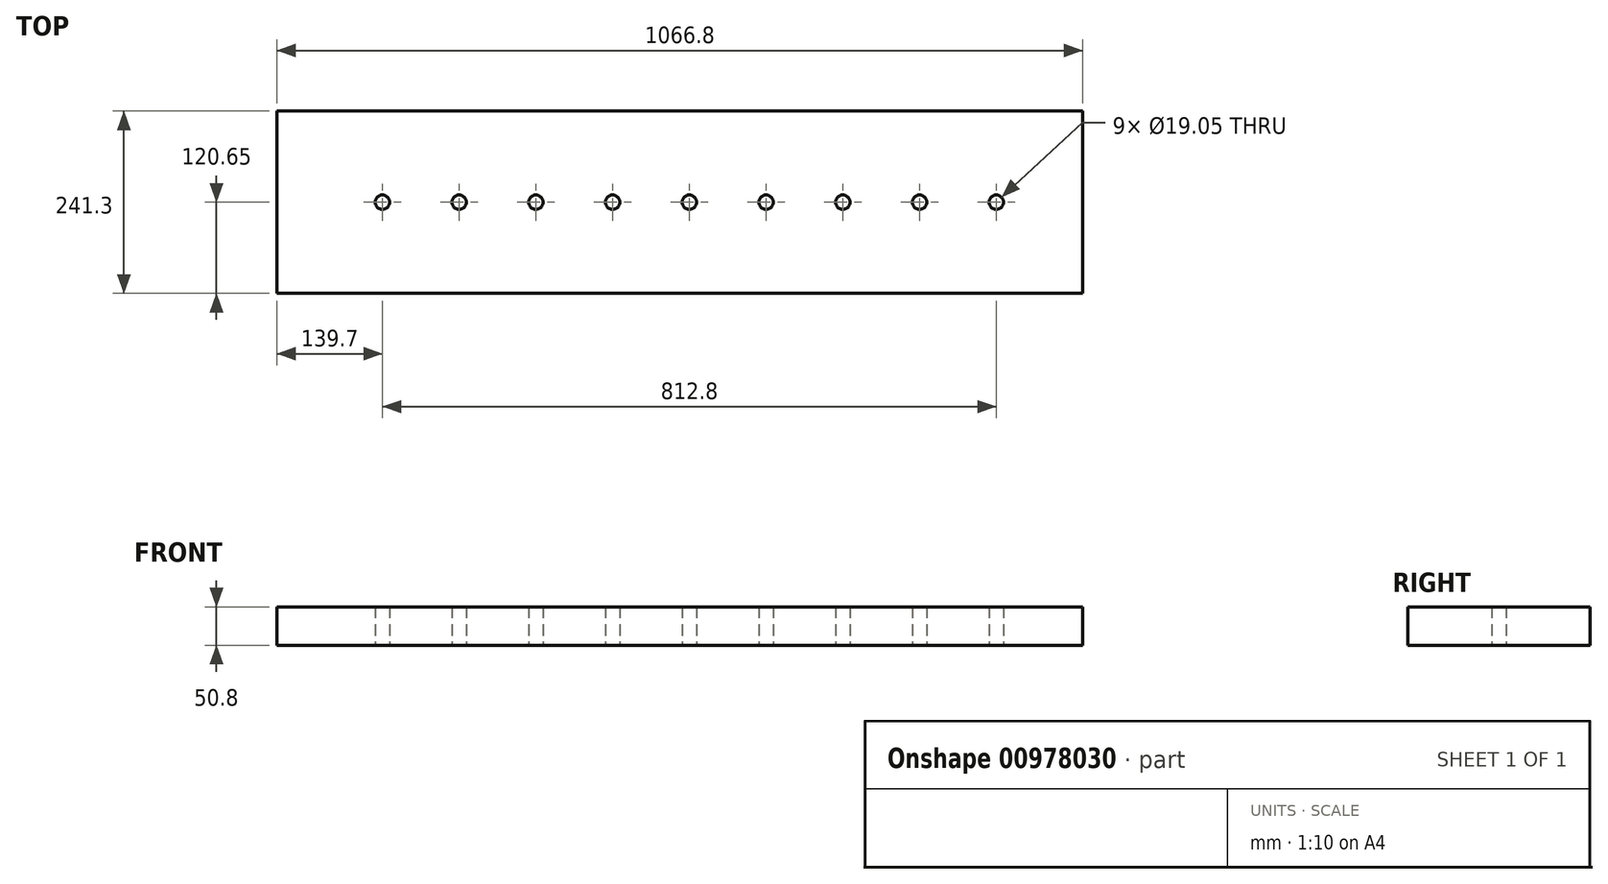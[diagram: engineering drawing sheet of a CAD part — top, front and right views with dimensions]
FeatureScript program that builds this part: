
annotation { "Feature Type Name" : "Feature", "Feature Type Description" : "" }
export const myFeature = defineFeature(function(context is Context, id is Id, definition is map)
    precondition{}
    {
        {
            var Q0;
            Q0=qCreatedBy(makeId("Top.planeOp"),FACE);
            var sketch = newSketch(context, id + "F0", { "sketchPlane" : qUnion([Q0])});
            skLineSegment(sketch, "E0", {"start": v(-533.4, 0) * mm, "end": v(533.4, 0) * mm, "construction": true});
            skLineSegment(sketch, "E1", {"start": v(0, 120.65) * mm, "end": v(0, -120.65) * mm, "construction": true});
            skLineSegment(sketch, "E2.bottom", {"start": v(-533.4, 120.65) * mm, "end": v(533.4, 120.65) * mm});
            skLineSegment(sketch, "E2.top", {"start": v(-533.4, -120.65) * mm, "end": v(533.4, -120.65) * mm});
            skLineSegment(sketch, "E2.left", {"start": v(-533.4, 120.65) * mm, "end": v(-533.4, -120.65) * mm});
            skLineSegment(sketch, "E2.right", {"start": v(533.4, 120.65) * mm, "end": v(533.4, -120.65) * mm});
            skCircle(sketch, "E3", {"center": v(-393.7, 0) * mm, "radius": 9.53 * mm});
            skCircle(sketch, "E4.1.0.0", {"center": v(-292.1, 0) * mm, "radius": 9.53 * mm});
            skCircle(sketch, "E4.2.0.0", {"center": v(-190.5, 0) * mm, "radius": 9.53 * mm});
            skCircle(sketch, "E4.3.0.0", {"center": v(-88.9, 0) * mm, "radius": 9.53 * mm});
            skCircle(sketch, "E4.4.0.0", {"center": v(12.7, 0) * mm, "radius": 9.53 * mm});
            skCircle(sketch, "E4.5.0.0", {"center": v(114.3, 0) * mm, "radius": 9.53 * mm});
            skCircle(sketch, "E4.6.0.0", {"center": v(215.9, 0) * mm, "radius": 9.53 * mm});
            skCircle(sketch, "E4.7.0.0", {"center": v(317.5, 0) * mm, "radius": 9.53 * mm});
            skCircle(sketch, "E4.8.0.0", {"center": v(419.1, 0) * mm, "radius": 9.53 * mm});
            skLineSegment(sketch, "E4.direction1", {"start": v(-393.7, 0) * mm, "end": v(-292.1, 0) * mm, "construction": true});
            skSolve(sketch);
        }
        {
            var Q0;
            Q0=makeQuery(id+"F0.imprint","IMPRINT",FACE,{"disambiguationData":[TD([[makeQuery(id+"F0.imprint","IMPRINT",EDGE,{"derivedFrom":sQuery(id+"F0.wireOp",EDGE,"E2.bottom")}),-1.0]])]});
            extrude(context, id + "F1", {"entities" : qUnion([Q0]), "depth" : 50.8 * mm, "offsetDistance" : 25.4 * mm});
        }
    });
